# Revit family: Door_Overhead_WD_High-Speed-Doors-887
name_source: partatom
category: Doors
revit_build: Autodesk Revit 2018 (Build: 20190510_1515(x64)
units: mm (PartAtom-declared; Revit-internal decimal feet)

## family parameters
Always vertical = Yes
Cut with Voids When Loaded = No
Host = Wall
OmniClass Number = 23.30.10.00
OmniClass Title = Doors
Room Calculation Point = No
Shared = No

## types (3) — shared parameters
A = 42 "
B = 31.63 "
C = 22.32 "
CAD Details = https://www.arcat.com
Curtain Shutter = Finishes - Curtain Shutter
D = 14.53 "
E = 14.09 "
Height = 216 "
Keynote = 08 33 23
Manufacturer Website = https://www.wayne-dalton.com
Min Max Height = 4' 0" - 18' -0"
Min Max Width = 4' 0" - 12' -0"
Product Data = https://www.arcat.com
Side Cover = Finishes - Side Cover
Specification = https://www.arcat.com
Top Box = Finishes - Top Box
URL = https://www.wayne-dalton.com
Wall Closure = By host
Width = 120 "
zero-valued in all types: Rough Height, Rough Width, Thickness

## per-type parameters (varying)
| type | Air Curtain |
| High Speed Freezer Door 887 - Heated Air Curtain | Yes |
| High Speed Freezer Door 887 - Without Air Curtain | No |
| High Speed Freezer Door 887 - Ambient Air Curtain | Yes |

note: column(s) folded — value = type name in every type: Model

## geometry (parser evidence)
native form markers: Sweep x10
no freeform markers — native parametric forms only
